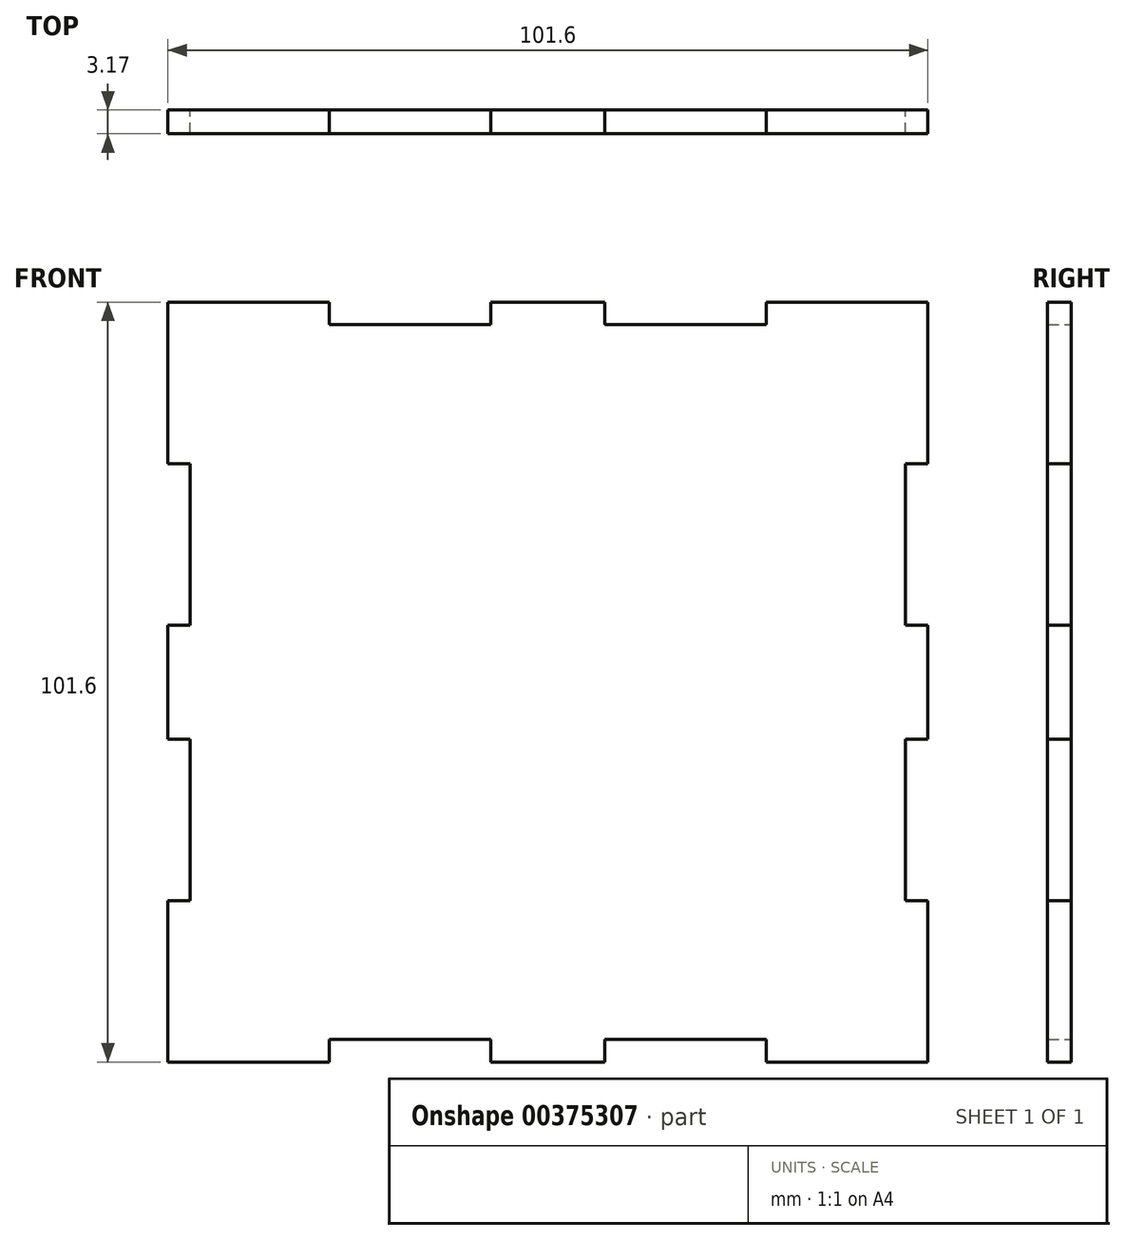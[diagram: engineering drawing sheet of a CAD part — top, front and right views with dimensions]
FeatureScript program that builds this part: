
annotation { "Feature Type Name" : "Feature", "Feature Type Description" : "" }
export const myFeature = defineFeature(function(context is Context, id is Id, definition is map)
    precondition{}
    {
        {
            var Q0;
            Q0=qCreatedBy(makeId("Front.planeOp"),FACE);
            var sketch = newSketch(context, id + "F0", { "sketchPlane" : qUnion([Q0])});
            skLineSegment(sketch, "E0", {"start": v(-152.4, 101.6) * mm, "end": v(-130.8, 101.6) * mm});
            skLineSegment(sketch, "E1", {"start": v(-130.8, 101.6) * mm, "end": v(-130.8, 98.6) * mm});
            skLineSegment(sketch, "E2", {"start": v(-130.8, 98.6) * mm, "end": v(-109.22, 98.6) * mm});
            skLineSegment(sketch, "E3", {"start": v(-109.22, 98.6) * mm, "end": v(-109.22, 101.6) * mm});
            skLineSegment(sketch, "E4", {"start": v(-109.22, 101.6) * mm, "end": v(-93.98, 101.6) * mm});
            skLineSegment(sketch, "E5", {"start": v(-93.98, 101.6) * mm, "end": v(-93.98, 98.6) * mm});
            skLineSegment(sketch, "E6", {"start": v(-93.98, 98.6) * mm, "end": v(-72.4, 98.6) * mm});
            skLineSegment(sketch, "E7", {"start": v(-72.4, 98.6) * mm, "end": v(-72.4, 101.6) * mm});
            skLineSegment(sketch, "E8", {"start": v(-72.4, 101.6) * mm, "end": v(-50.8, 101.6) * mm});
            skLineSegment(sketch, "E9", {"start": v(-50.8, 101.6) * mm, "end": v(-50.8, 80.01) * mm});
            skLineSegment(sketch, "E10", {"start": v(-50.8, 80.01) * mm, "end": v(-53.8, 80.01) * mm});
            skLineSegment(sketch, "E11", {"start": v(-53.8, 80.01) * mm, "end": v(-53.8, 58.42) * mm});
            skLineSegment(sketch, "E12", {"start": v(-53.8, 58.42) * mm, "end": v(-50.8, 58.42) * mm});
            skLineSegment(sketch, "E13", {"start": v(-50.8, 58.42) * mm, "end": v(-50.8, 43.18) * mm});
            skLineSegment(sketch, "E14", {"start": v(-50.8, 43.18) * mm, "end": v(-53.8, 43.18) * mm});
            skLineSegment(sketch, "E15", {"start": v(-53.8, 43.18) * mm, "end": v(-53.8, 21.59) * mm});
            skLineSegment(sketch, "E16", {"start": v(-53.8, 21.59) * mm, "end": v(-50.8, 21.59) * mm});
            skLineSegment(sketch, "E17", {"start": v(-50.8, 21.59) * mm, "end": v(-50.8, 0) * mm});
            skLineSegment(sketch, "E18", {"start": v(-50.8, 0) * mm, "end": v(-72.4, 0) * mm});
            skLineSegment(sketch, "E19", {"start": v(-72.4, 0) * mm, "end": v(-72.4, 3) * mm});
            skLineSegment(sketch, "E20", {"start": v(-72.4, 3) * mm, "end": v(-93.98, 3) * mm});
            skLineSegment(sketch, "E21", {"start": v(-93.98, 3) * mm, "end": v(-93.98, 0) * mm});
            skLineSegment(sketch, "E22", {"start": v(-93.98, 0) * mm, "end": v(-109.22, 0) * mm});
            skLineSegment(sketch, "E23", {"start": v(-109.22, 0) * mm, "end": v(-109.22, 3) * mm});
            skLineSegment(sketch, "E24", {"start": v(-109.22, 3) * mm, "end": v(-130.8, 3) * mm});
            skLineSegment(sketch, "E25", {"start": v(-130.8, 3) * mm, "end": v(-130.8, 0) * mm});
            skLineSegment(sketch, "E26", {"start": v(-130.8, 0) * mm, "end": v(-152.4, 0) * mm});
            skLineSegment(sketch, "E27", {"start": v(-152.4, 0) * mm, "end": v(-152.4, 21.59) * mm});
            skLineSegment(sketch, "E28", {"start": v(-152.4, 21.59) * mm, "end": v(-149.4, 21.59) * mm});
            skLineSegment(sketch, "E29", {"start": v(-149.4, 21.59) * mm, "end": v(-149.4, 43.18) * mm});
            skLineSegment(sketch, "E30", {"start": v(-149.4, 43.18) * mm, "end": v(-152.4, 43.18) * mm});
            skLineSegment(sketch, "E31", {"start": v(-152.4, 43.18) * mm, "end": v(-152.4, 58.42) * mm});
            skLineSegment(sketch, "E32", {"start": v(-152.4, 58.42) * mm, "end": v(-149.4, 58.42) * mm});
            skLineSegment(sketch, "E33", {"start": v(-149.4, 58.42) * mm, "end": v(-149.4, 80.01) * mm});
            skLineSegment(sketch, "E34", {"start": v(-149.4, 80.01) * mm, "end": v(-152.4, 80.01) * mm});
            skLineSegment(sketch, "E35", {"start": v(-152.4, 80.01) * mm, "end": v(-152.4, 101.6) * mm});
            skLineSegment(sketch, "E36", {"start": v(-50.8, 101.6) * mm, "end": v(-29.21, 101.6) * mm});
            skLineSegment(sketch, "E37", {"start": v(-29.21, 101.6) * mm, "end": v(-29.21, 98.6) * mm});
            skLineSegment(sketch, "E38", {"start": v(-29.21, 98.6) * mm, "end": v(-7.62, 98.6) * mm});
            skLineSegment(sketch, "E39", {"start": v(-7.62, 98.6) * mm, "end": v(-7.62, 101.6) * mm});
            skLineSegment(sketch, "E40", {"start": v(-7.62, 101.6) * mm, "end": v(7.62, 101.6) * mm});
            skLineSegment(sketch, "E41", {"start": v(7.62, 101.6) * mm, "end": v(7.62, 98.6) * mm});
            skLineSegment(sketch, "E42", {"start": v(7.62, 98.6) * mm, "end": v(29.21, 98.6) * mm});
            skLineSegment(sketch, "E43", {"start": v(29.21, 98.6) * mm, "end": v(29.21, 101.6) * mm});
            skLineSegment(sketch, "E44", {"start": v(29.21, 101.6) * mm, "end": v(50.8, 101.6) * mm});
            skLineSegment(sketch, "E45", {"start": v(50.8, 101.6) * mm, "end": v(50.8, 80.01) * mm});
            skLineSegment(sketch, "E46", {"start": v(50.8, 80.01) * mm, "end": v(47.8, 80.01) * mm});
            skLineSegment(sketch, "E47", {"start": v(47.8, 80.01) * mm, "end": v(47.8, 58.42) * mm});
            skLineSegment(sketch, "E48", {"start": v(47.8, 58.42) * mm, "end": v(50.8, 58.42) * mm});
            skLineSegment(sketch, "E49", {"start": v(50.8, 58.42) * mm, "end": v(50.8, 43.18) * mm});
            skLineSegment(sketch, "E50", {"start": v(50.8, 43.18) * mm, "end": v(47.8, 43.18) * mm});
            skLineSegment(sketch, "E51", {"start": v(47.8, 43.18) * mm, "end": v(47.8, 21.59) * mm});
            skLineSegment(sketch, "E52", {"start": v(47.8, 21.59) * mm, "end": v(50.8, 21.59) * mm});
            skLineSegment(sketch, "E53", {"start": v(50.8, 21.59) * mm, "end": v(50.8, 0) * mm});
            skLineSegment(sketch, "E54", {"start": v(50.8, 0) * mm, "end": v(29.21, 0) * mm});
            skLineSegment(sketch, "E55", {"start": v(29.21, 0) * mm, "end": v(29.21, 3) * mm});
            skLineSegment(sketch, "E56", {"start": v(29.21, 3) * mm, "end": v(7.62, 3) * mm});
            skLineSegment(sketch, "E57", {"start": v(7.62, 3) * mm, "end": v(7.62, 0) * mm});
            skLineSegment(sketch, "E58", {"start": v(7.62, 0) * mm, "end": v(-7.62, 0) * mm});
            skLineSegment(sketch, "E59", {"start": v(-7.62, 0) * mm, "end": v(-7.62, 3) * mm});
            skLineSegment(sketch, "E60", {"start": v(-7.62, 3) * mm, "end": v(-29.21, 3) * mm});
            skLineSegment(sketch, "E61", {"start": v(-29.21, 3) * mm, "end": v(-29.21, 0) * mm});
            skLineSegment(sketch, "E62", {"start": v(-29.21, 0) * mm, "end": v(-50.8, 0) * mm});
            skLineSegment(sketch, "E63", {"start": v(-50.8, 0) * mm, "end": v(-50.8, 21.59) * mm});
            skLineSegment(sketch, "E64", {"start": v(-50.8, 21.59) * mm, "end": v(-47.8, 21.59) * mm});
            skLineSegment(sketch, "E65", {"start": v(-47.8, 21.59) * mm, "end": v(-47.8, 43.18) * mm});
            skLineSegment(sketch, "E66", {"start": v(-47.8, 43.18) * mm, "end": v(-50.8, 43.18) * mm});
            skLineSegment(sketch, "E67", {"start": v(-50.8, 43.18) * mm, "end": v(-50.8, 58.42) * mm});
            skLineSegment(sketch, "E68", {"start": v(-50.8, 58.42) * mm, "end": v(-47.8, 58.42) * mm});
            skLineSegment(sketch, "E69", {"start": v(-47.8, 58.42) * mm, "end": v(-47.8, 80.01) * mm});
            skLineSegment(sketch, "E70", {"start": v(-47.8, 80.01) * mm, "end": v(-50.8, 80.01) * mm});
            skLineSegment(sketch, "E71", {"start": v(-50.8, 80.01) * mm, "end": v(-50.8, 101.6) * mm});
            skLineSegment(sketch, "E72", {"start": v(53.8, 101.6) * mm, "end": v(72.39, 101.6) * mm});
            skLineSegment(sketch, "E73", {"start": v(72.39, 101.6) * mm, "end": v(72.39, 98.6) * mm});
            skLineSegment(sketch, "E74", {"start": v(72.39, 98.6) * mm, "end": v(93.98, 98.6) * mm});
            skLineSegment(sketch, "E75", {"start": v(93.98, 98.6) * mm, "end": v(93.98, 101.6) * mm});
            skLineSegment(sketch, "E76", {"start": v(93.98, 101.6) * mm, "end": v(109.22, 101.6) * mm});
            skLineSegment(sketch, "E77", {"start": v(109.22, 101.6) * mm, "end": v(109.22, 98.6) * mm});
            skLineSegment(sketch, "E78", {"start": v(109.22, 98.6) * mm, "end": v(130.8, 98.6) * mm});
            skLineSegment(sketch, "E79", {"start": v(130.8, 98.6) * mm, "end": v(130.8, 101.6) * mm});
            skLineSegment(sketch, "E80", {"start": v(130.8, 101.6) * mm, "end": v(149.4, 101.6) * mm});
            skLineSegment(sketch, "E81", {"start": v(149.4, 101.6) * mm, "end": v(149.4, 80.01) * mm});
            skLineSegment(sketch, "E82", {"start": v(149.4, 80.01) * mm, "end": v(152.4, 80.01) * mm});
            skLineSegment(sketch, "E83", {"start": v(152.4, 80.01) * mm, "end": v(152.4, 58.42) * mm});
            skLineSegment(sketch, "E84", {"start": v(152.4, 58.42) * mm, "end": v(149.4, 58.42) * mm});
            skLineSegment(sketch, "E85", {"start": v(149.4, 58.42) * mm, "end": v(149.4, 43.18) * mm});
            skLineSegment(sketch, "E86", {"start": v(149.4, 43.18) * mm, "end": v(152.4, 43.18) * mm});
            skLineSegment(sketch, "E87", {"start": v(152.4, 43.18) * mm, "end": v(152.4, 21.59) * mm});
            skLineSegment(sketch, "E88", {"start": v(152.4, 21.59) * mm, "end": v(149.4, 21.59) * mm});
            skLineSegment(sketch, "E89", {"start": v(149.4, 21.59) * mm, "end": v(149.4, 0) * mm});
            skLineSegment(sketch, "E90", {"start": v(149.4, 0) * mm, "end": v(130.8, 0) * mm});
            skLineSegment(sketch, "E91", {"start": v(130.8, 0) * mm, "end": v(130.8, 3) * mm});
            skLineSegment(sketch, "E92", {"start": v(130.8, 3) * mm, "end": v(109.22, 3) * mm});
            skLineSegment(sketch, "E93", {"start": v(109.22, 3) * mm, "end": v(109.22, 0) * mm});
            skLineSegment(sketch, "E94", {"start": v(109.22, 0) * mm, "end": v(93.98, 0) * mm});
            skLineSegment(sketch, "E95", {"start": v(93.98, 0) * mm, "end": v(93.98, 3) * mm});
            skLineSegment(sketch, "E96", {"start": v(93.98, 3) * mm, "end": v(72.39, 3) * mm});
            skLineSegment(sketch, "E97", {"start": v(72.39, 3) * mm, "end": v(72.39, 0) * mm});
            skLineSegment(sketch, "E98", {"start": v(72.39, 0) * mm, "end": v(53.8, 0) * mm});
            skLineSegment(sketch, "E99", {"start": v(53.8, 0) * mm, "end": v(53.8, 21.59) * mm});
            skLineSegment(sketch, "E100", {"start": v(53.8, 21.59) * mm, "end": v(50.8, 21.59) * mm});
            skLineSegment(sketch, "E101", {"start": v(50.8, 21.59) * mm, "end": v(50.8, 43.18) * mm});
            skLineSegment(sketch, "E102", {"start": v(50.8, 43.18) * mm, "end": v(53.8, 43.18) * mm});
            skLineSegment(sketch, "E103", {"start": v(53.8, 43.18) * mm, "end": v(53.8, 58.42) * mm});
            skLineSegment(sketch, "E104", {"start": v(53.8, 58.42) * mm, "end": v(50.8, 58.42) * mm});
            skLineSegment(sketch, "E105", {"start": v(50.8, 58.42) * mm, "end": v(50.8, 80.01) * mm});
            skLineSegment(sketch, "E106", {"start": v(50.8, 80.01) * mm, "end": v(53.8, 80.01) * mm});
            skLineSegment(sketch, "E107", {"start": v(53.8, 80.01) * mm, "end": v(53.8, 101.6) * mm});
            skLineSegment(sketch, "E108", {"start": v(53.8, 0) * mm, "end": v(72.39, 0) * mm});
            skLineSegment(sketch, "E109", {"start": v(72.39, 0) * mm, "end": v(72.39, -3) * mm});
            skLineSegment(sketch, "E110", {"start": v(72.39, -3) * mm, "end": v(93.98, -3) * mm});
            skLineSegment(sketch, "E111", {"start": v(93.98, -3) * mm, "end": v(93.98, 0) * mm});
            skLineSegment(sketch, "E112", {"start": v(93.98, 0) * mm, "end": v(109.22, 0) * mm});
            skLineSegment(sketch, "E113", {"start": v(109.22, 0) * mm, "end": v(109.22, -3) * mm});
            skLineSegment(sketch, "E114", {"start": v(109.22, -3) * mm, "end": v(130.8, -3) * mm});
            skLineSegment(sketch, "E115", {"start": v(130.8, -3) * mm, "end": v(130.8, 0) * mm});
            skLineSegment(sketch, "E116", {"start": v(130.8, 0) * mm, "end": v(149.4, 0) * mm});
            skLineSegment(sketch, "E117", {"start": v(149.4, 0) * mm, "end": v(149.4, -21.6) * mm});
            skLineSegment(sketch, "E118", {"start": v(149.4, -21.6) * mm, "end": v(152.4, -21.6) * mm});
            skLineSegment(sketch, "E119", {"start": v(152.4, -21.6) * mm, "end": v(152.4, -43.18) * mm});
            skLineSegment(sketch, "E120", {"start": v(152.4, -43.18) * mm, "end": v(149.4, -43.18) * mm});
            skLineSegment(sketch, "E121", {"start": v(149.4, -43.18) * mm, "end": v(149.4, -58.42) * mm});
            skLineSegment(sketch, "E122", {"start": v(149.4, -58.42) * mm, "end": v(152.4, -58.42) * mm});
            skLineSegment(sketch, "E123", {"start": v(152.4, -58.42) * mm, "end": v(152.4, -80.01) * mm});
            skLineSegment(sketch, "E124", {"start": v(152.4, -80.01) * mm, "end": v(149.4, -80.01) * mm});
            skLineSegment(sketch, "E125", {"start": v(149.4, -80.01) * mm, "end": v(149.4, -101.6) * mm});
            skLineSegment(sketch, "E126", {"start": v(149.4, -101.6) * mm, "end": v(130.8, -101.6) * mm});
            skLineSegment(sketch, "E127", {"start": v(130.8, -101.6) * mm, "end": v(130.8, -98.6) * mm});
            skLineSegment(sketch, "E128", {"start": v(130.8, -98.6) * mm, "end": v(109.22, -98.6) * mm});
            skLineSegment(sketch, "E129", {"start": v(109.22, -98.6) * mm, "end": v(109.22, -101.6) * mm});
            skLineSegment(sketch, "E130", {"start": v(109.22, -101.6) * mm, "end": v(93.98, -101.6) * mm});
            skLineSegment(sketch, "E131", {"start": v(93.98, -101.6) * mm, "end": v(93.98, -98.6) * mm});
            skLineSegment(sketch, "E132", {"start": v(93.98, -98.6) * mm, "end": v(72.39, -98.6) * mm});
            skLineSegment(sketch, "E133", {"start": v(72.39, -98.6) * mm, "end": v(72.39, -101.6) * mm});
            skLineSegment(sketch, "E134", {"start": v(72.39, -101.6) * mm, "end": v(53.8, -101.6) * mm});
            skLineSegment(sketch, "E135", {"start": v(53.8, -101.6) * mm, "end": v(53.8, -80.01) * mm});
            skLineSegment(sketch, "E136", {"start": v(53.8, -80.01) * mm, "end": v(50.8, -80.01) * mm});
            skLineSegment(sketch, "E137", {"start": v(50.8, -80.01) * mm, "end": v(50.8, -58.42) * mm});
            skLineSegment(sketch, "E138", {"start": v(50.8, -58.42) * mm, "end": v(53.8, -58.42) * mm});
            skLineSegment(sketch, "E139", {"start": v(53.8, -58.42) * mm, "end": v(53.8, -43.18) * mm});
            skLineSegment(sketch, "E140", {"start": v(53.8, -43.18) * mm, "end": v(50.8, -43.18) * mm});
            skLineSegment(sketch, "E141", {"start": v(50.8, -43.18) * mm, "end": v(50.8, -21.6) * mm});
            skLineSegment(sketch, "E142", {"start": v(50.8, -21.6) * mm, "end": v(53.8, -21.6) * mm});
            skLineSegment(sketch, "E143", {"start": v(53.8, -21.6) * mm, "end": v(53.8, 0) * mm});
            skLineSegment(sketch, "E144", {"start": v(-149.4, -3) * mm, "end": v(-130.8, -3) * mm});
            skLineSegment(sketch, "E145", {"start": v(-130.8, -3) * mm, "end": v(-130.8, 0) * mm});
            skLineSegment(sketch, "E146", {"start": v(-130.8, 0) * mm, "end": v(-109.22, 0) * mm});
            skLineSegment(sketch, "E147", {"start": v(-109.22, 0) * mm, "end": v(-109.22, -3) * mm});
            skLineSegment(sketch, "E148", {"start": v(-109.22, -3) * mm, "end": v(-93.98, -3) * mm});
            skLineSegment(sketch, "E149", {"start": v(-93.98, -3) * mm, "end": v(-93.98, 0) * mm});
            skLineSegment(sketch, "E150", {"start": v(-93.98, 0) * mm, "end": v(-72.4, 0) * mm});
            skLineSegment(sketch, "E151", {"start": v(-72.4, 0) * mm, "end": v(-72.4, -3) * mm});
            skLineSegment(sketch, "E152", {"start": v(-72.4, -3) * mm, "end": v(-53.8, -3) * mm});
            skLineSegment(sketch, "E153", {"start": v(-53.8, -3) * mm, "end": v(-53.8, -21.6) * mm});
            skLineSegment(sketch, "E154", {"start": v(-53.8, -21.6) * mm, "end": v(-50.8, -21.6) * mm});
            skLineSegment(sketch, "E155", {"start": v(-50.8, -21.6) * mm, "end": v(-50.8, -43.18) * mm});
            skLineSegment(sketch, "E156", {"start": v(-50.8, -43.18) * mm, "end": v(-53.8, -43.18) * mm});
            skLineSegment(sketch, "E157", {"start": v(-53.8, -43.18) * mm, "end": v(-53.8, -58.42) * mm});
            skLineSegment(sketch, "E158", {"start": v(-53.8, -58.42) * mm, "end": v(-50.8, -58.42) * mm});
            skLineSegment(sketch, "E159", {"start": v(-50.8, -58.42) * mm, "end": v(-50.8, -80.01) * mm});
            skLineSegment(sketch, "E160", {"start": v(-50.8, -80.01) * mm, "end": v(-53.8, -80.01) * mm});
            skLineSegment(sketch, "E161", {"start": v(-53.8, -80.01) * mm, "end": v(-53.8, -98.6) * mm});
            skLineSegment(sketch, "E162", {"start": v(-53.8, -98.6) * mm, "end": v(-72.4, -98.6) * mm});
            skLineSegment(sketch, "E163", {"start": v(-72.4, -98.6) * mm, "end": v(-72.4, -101.6) * mm});
            skLineSegment(sketch, "E164", {"start": v(-72.4, -101.6) * mm, "end": v(-93.98, -101.6) * mm});
            skLineSegment(sketch, "E165", {"start": v(-93.98, -101.6) * mm, "end": v(-93.98, -98.6) * mm});
            skLineSegment(sketch, "E166", {"start": v(-93.98, -98.6) * mm, "end": v(-109.22, -98.6) * mm});
            skLineSegment(sketch, "E167", {"start": v(-109.22, -98.6) * mm, "end": v(-109.22, -101.6) * mm});
            skLineSegment(sketch, "E168", {"start": v(-109.22, -101.6) * mm, "end": v(-130.8, -101.6) * mm});
            skLineSegment(sketch, "E169", {"start": v(-130.8, -101.6) * mm, "end": v(-130.8, -98.6) * mm});
            skLineSegment(sketch, "E170", {"start": v(-130.8, -98.6) * mm, "end": v(-149.4, -98.6) * mm});
            skLineSegment(sketch, "E171", {"start": v(-149.4, -98.6) * mm, "end": v(-149.4, -80.01) * mm});
            skLineSegment(sketch, "E172", {"start": v(-149.4, -80.01) * mm, "end": v(-152.4, -80.01) * mm});
            skLineSegment(sketch, "E173", {"start": v(-152.4, -80.01) * mm, "end": v(-152.4, -58.42) * mm});
            skLineSegment(sketch, "E174", {"start": v(-152.4, -58.42) * mm, "end": v(-149.4, -58.42) * mm});
            skLineSegment(sketch, "E175", {"start": v(-149.4, -58.42) * mm, "end": v(-149.4, -43.18) * mm});
            skLineSegment(sketch, "E176", {"start": v(-149.4, -43.18) * mm, "end": v(-152.4, -43.18) * mm});
            skLineSegment(sketch, "E177", {"start": v(-152.4, -43.18) * mm, "end": v(-152.4, -21.6) * mm});
            skLineSegment(sketch, "E178", {"start": v(-152.4, -21.6) * mm, "end": v(-149.4, -21.6) * mm});
            skLineSegment(sketch, "E179", {"start": v(-149.4, -21.6) * mm, "end": v(-149.4, -3) * mm});
            skLineSegment(sketch, "E180", {"start": v(-47.8, -3) * mm, "end": v(-29.21, -3) * mm});
            skLineSegment(sketch, "E181", {"start": v(-29.21, -3) * mm, "end": v(-29.21, 0) * mm});
            skLineSegment(sketch, "E182", {"start": v(-29.21, 0) * mm, "end": v(-7.62, 0) * mm});
            skLineSegment(sketch, "E183", {"start": v(-7.62, 0) * mm, "end": v(-7.62, -3) * mm});
            skLineSegment(sketch, "E184", {"start": v(-7.62, -3) * mm, "end": v(7.62, -3) * mm});
            skLineSegment(sketch, "E185", {"start": v(7.62, -3) * mm, "end": v(7.62, 0) * mm});
            skLineSegment(sketch, "E186", {"start": v(7.62, 0) * mm, "end": v(29.21, 0) * mm});
            skLineSegment(sketch, "E187", {"start": v(29.21, 0) * mm, "end": v(29.21, -3) * mm});
            skLineSegment(sketch, "E188", {"start": v(29.21, -3) * mm, "end": v(47.8, -3) * mm});
            skLineSegment(sketch, "E189", {"start": v(47.8, -3) * mm, "end": v(47.8, -21.6) * mm});
            skLineSegment(sketch, "E190", {"start": v(47.8, -21.6) * mm, "end": v(50.8, -21.6) * mm});
            skLineSegment(sketch, "E191", {"start": v(50.8, -21.6) * mm, "end": v(50.8, -43.18) * mm});
            skLineSegment(sketch, "E192", {"start": v(50.8, -43.18) * mm, "end": v(47.8, -43.18) * mm});
            skLineSegment(sketch, "E193", {"start": v(47.8, -43.18) * mm, "end": v(47.8, -58.42) * mm});
            skLineSegment(sketch, "E194", {"start": v(47.8, -58.42) * mm, "end": v(50.8, -58.42) * mm});
            skLineSegment(sketch, "E195", {"start": v(50.8, -58.42) * mm, "end": v(50.8, -80.01) * mm});
            skLineSegment(sketch, "E196", {"start": v(50.8, -80.01) * mm, "end": v(47.8, -80.01) * mm});
            skLineSegment(sketch, "E197", {"start": v(47.8, -80.01) * mm, "end": v(47.8, -98.6) * mm});
            skLineSegment(sketch, "E198", {"start": v(47.8, -98.6) * mm, "end": v(29.21, -98.6) * mm});
            skLineSegment(sketch, "E199", {"start": v(29.21, -98.6) * mm, "end": v(29.21, -101.6) * mm});
            skLineSegment(sketch, "E200", {"start": v(29.21, -101.6) * mm, "end": v(7.62, -101.6) * mm});
            skLineSegment(sketch, "E201", {"start": v(7.62, -101.6) * mm, "end": v(7.62, -98.6) * mm});
            skLineSegment(sketch, "E202", {"start": v(7.62, -98.6) * mm, "end": v(-7.62, -98.6) * mm});
            skLineSegment(sketch, "E203", {"start": v(-7.62, -98.6) * mm, "end": v(-7.62, -101.6) * mm});
            skLineSegment(sketch, "E204", {"start": v(-7.62, -101.6) * mm, "end": v(-29.21, -101.6) * mm});
            skLineSegment(sketch, "E205", {"start": v(-29.21, -101.6) * mm, "end": v(-29.21, -98.6) * mm});
            skLineSegment(sketch, "E206", {"start": v(-29.21, -98.6) * mm, "end": v(-47.8, -98.6) * mm});
            skLineSegment(sketch, "E207", {"start": v(-47.8, -98.6) * mm, "end": v(-47.8, -80.01) * mm});
            skLineSegment(sketch, "E208", {"start": v(-47.8, -80.01) * mm, "end": v(-50.8, -80.01) * mm});
            skLineSegment(sketch, "E209", {"start": v(-50.8, -80.01) * mm, "end": v(-50.8, -58.42) * mm});
            skLineSegment(sketch, "E210", {"start": v(-50.8, -58.42) * mm, "end": v(-47.8, -58.42) * mm});
            skLineSegment(sketch, "E211", {"start": v(-47.8, -58.42) * mm, "end": v(-47.8, -43.18) * mm});
            skLineSegment(sketch, "E212", {"start": v(-47.8, -43.18) * mm, "end": v(-50.8, -43.18) * mm});
            skLineSegment(sketch, "E213", {"start": v(-50.8, -43.18) * mm, "end": v(-50.8, -21.6) * mm});
            skLineSegment(sketch, "E214", {"start": v(-50.8, -21.6) * mm, "end": v(-47.8, -21.6) * mm});
            skLineSegment(sketch, "E215", {"start": v(-47.8, -21.6) * mm, "end": v(-47.8, -3) * mm});
            skSolve(sketch);
        }
        {
            var Q0;
            Q0=makeQuery(id+"F0.imprint","IMPRINT",FACE,{"disambiguationData":[TD([[makeQuery(id+"F0.imprint","IMPRINT",EDGE,{"derivedFrom":sQuery(id+"F0.wireOp",EDGE,"E0")}),-1.0]])]});
            extrude(context, id + "F1", {"entities" : qUnion([Q0]), "depth" : 3.17 * mm});
        }
    });
